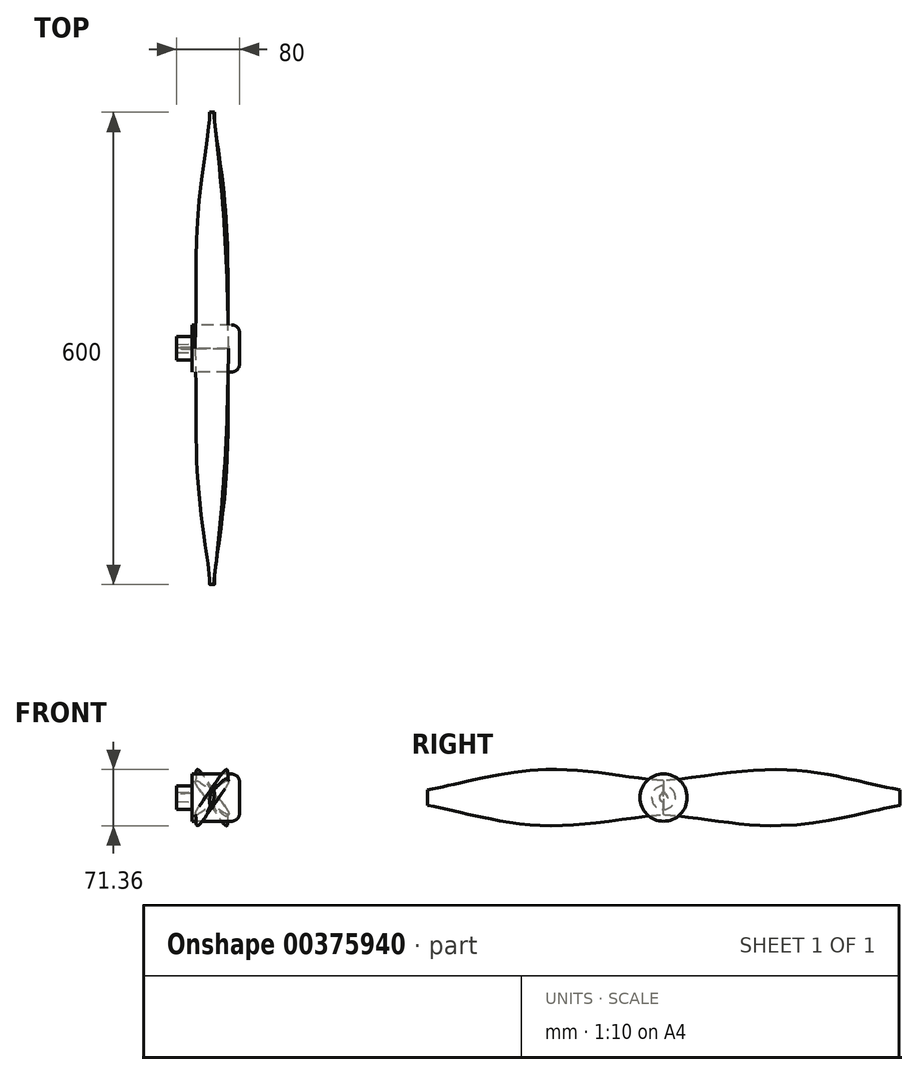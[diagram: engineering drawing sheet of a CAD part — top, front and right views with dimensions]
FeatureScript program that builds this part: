
annotation { "Feature Type Name" : "Feature", "Feature Type Description" : "" }
export const myFeature = defineFeature(function(context is Context, id is Id, definition is map)
    precondition{}
    {
        {
            var Q0;
            Q0=qCreatedBy(makeId("Front.planeOp"),FACE);
            var sketch = newSketch(context, id + "F0", { "sketchPlane" : qUnion([Q0])});
            skEllipse(sketch, "E0", {"center": v(0, 0) * mm, "majorRadius": 30 * mm, "minorRadius": 5 * mm, "majorAxis": v(0.7, 0.7)});
            skLineSegment(sketch, "E1", {"start": v(-3.54, 3.54) * mm, "end": v(3.54, -3.54) * mm, "construction": true});
            skLineSegment(sketch, "E2", {"start": v(-21.21, -21.21) * mm, "end": v(21.21, 21.21) * mm, "construction": true});
            skSolve(sketch);
        }
        {
            assignVariable(context, id + "F1", {"name" : "amplitude", "anyValue" : 300});
        }
        {
            var Q0;
            Q0=qCreatedBy(makeId("Front.planeOp"),FACE);
            cPlane(context, id + "F2", {"entities" : qUnion([Q0]), "cplaneType" : CPlaneType.OFFSET, "offset" : (getVariable(context, 'amplitude') / 2) * mm, "width" : 150 * mm, "height" : 150 * mm});
        }
        {
            var Q0;
            Q0=qCreatedBy(id+"F2.planeOp",FACE);
            var sketch = newSketch(context, id + "F3", { "sketchPlane" : qUnion([Q0])});
            skEllipse(sketch, "E3", {"center": v(0, 0) * mm, "majorRadius": 40 * mm, "minorRadius": 5 * mm, "majorAxis": v(0.46, 0.89)});
            skLineSegment(sketch, "E4", {"start": v(18.47, 35.48) * mm, "end": v(-18.47, -35.48) * mm, "construction": true});
            skLineSegment(sketch, "E5", {"start": v(-4.44, 2.3) * mm, "end": v(4.44, -2.3) * mm, "construction": true});
            skSolve(sketch);
        }
        {
            var Q0;
            Q0=qCreatedBy(makeId("Front.planeOp"),FACE);
            cPlane(context, id + "F4", {"entities" : qUnion([Q0]), "cplaneType" : CPlaneType.OFFSET, "offset" : (getVariable(context, 'amplitude')) * mm, "width" : 150 * mm, "height" : 150 * mm});
        }
        {
            var Q0;
            Q0=qCreatedBy(id+"F4.planeOp",FACE);
            var sketch = newSketch(context, id + "F5", { "sketchPlane" : qUnion([Q0])});
            skEllipse(sketch, "E6", {"center": v(0, 0) * mm, "majorRadius": 10 * mm, "minorRadius": 2.5 * mm, "majorAxis": v(0.17, 0.98)});
            skLineSegment(sketch, "E7", {"start": v(-1.74, -9.85) * mm, "end": v(1.74, 9.85) * mm, "construction": true});
            skLineSegment(sketch, "E8", {"start": v(-2.46, 0.43) * mm, "end": v(2.46, -0.43) * mm, "construction": true});
            skSolve(sketch);
        }
        {
            var Q0;
            Q0=qSketchRegion(id+"F0",true);
            var Q1;
            Q1=qSketchRegion(id+"F3",true);
            var Q2;
            Q2=qSketchRegion(id+"F5",true);
            loft(context, id + "F6", {"sheetProfilesArray" : [{ "sheetProfileEntities" : qUnion([Q0]) }, { "sheetProfileEntities" : qUnion([Q1]) }, { "sheetProfileEntities" : qUnion([Q2]) }]});
        }
        {
            var Q0;
            Q0=qCreatedBy(makeId("Front.planeOp"),FACE);
            var sketch = newSketch(context, id + "F7", { "sketchPlane" : qUnion([Q0])});
            skLineSegment(sketch, "E9", {"start": v(-64.42, 0) * mm, "end": v(60.6, 0) * mm, "construction": true});
            skSolve(sketch);
        }
        {
            var Q0;
            Q0=makeQuery(id+"F6.opLoft","SWEPT_BODY",BODY,{"disambiguationData":[OSD([makeQuery(id+"F0.imprint","IMPRINT",FACE,{"disambiguationData":[TD([[makeQuery(id+"F0.imprint","IMPRINT",EDGE,{"derivedFrom":sQuery(id+"F0.wireOp",EDGE,"E0")}),1.0]])]}),sQuery(id+"F3.wireOp",EDGE,"E3"),makeQuery(id+"F5.imprint","IMPRINT",FACE,{"disambiguationData":[TD([[makeQuery(id+"F5.imprint","IMPRINT",EDGE,{"derivedFrom":sQuery(id+"F5.wireOp",EDGE,"E6")}),1.0]])]})])]});
            var Q1;
            Q1=sQuery(id+"F7.wireOp",EDGE,"E9");
            circularPattern(context, id + "F8", {"entities" : qUnion([Q0]), "axis" : qUnion([Q1]), "angle" : 180 * degree, "instanceCount" : 2, "equalSpace" : true});
        }
        {
            var Q0;
            Q0=qCreatedBy(makeId("Front.planeOp"),FACE);
            var sketch = newSketch(context, id + "F9", { "sketchPlane" : qUnion([Q0])});
            skLineSegment(sketch, "E10", {"start": v(-45, 0) * mm, "end": v(35, 0) * mm});
            skLineSegment(sketch, "E11", {"start": v(35, 0) * mm, "end": v(35, 30) * mm});
            skLineSegment(sketch, "E12", {"start": v(35, 30) * mm, "end": v(-25, 30) * mm});
            skLineSegment(sketch, "E13", {"start": v(-25, 30) * mm, "end": v(-25, 15) * mm});
            skLineSegment(sketch, "E14", {"start": v(-25, 15) * mm, "end": v(-45, 15) * mm});
            skLineSegment(sketch, "E15", {"start": v(-45, 15) * mm, "end": v(-45, 0) * mm});
            skLineSegment(sketch, "E16", {"start": v(-61.67, 0) * mm, "end": v(55.31, 0) * mm, "construction": true});
            skSolve(sketch);
        }
        {
            var Q0;
            Q0=qSketchRegion(id+"F9",true);
            var Q1;
            Q1=sQuery(id+"F9.wireOp",EDGE,"E16");
            revolve(context, id + "F10", {"entities" : qUnion([Q0]), "axis" : qUnion([Q1]), "revolveType" : RevolveType.FULL});
        }
        {
            var Q0;
            Q0=makeQuery(id+"F10.opRevolve","SWEPT_EDGE",EDGE,{"disambiguationData":[OSD([sQuery(id+"F9.wireOp",EDGE,"E11"),sQuery(id+"F9.wireOp",EDGE,"E12")])]});
            fillet(context, id + "F11", {"entities" : qUnion([Q0]), "radius" : 10 * mm, "tangentPropagation" : true, "allowEdgeOverflow" : false});
        }
        {
            var Q0;
            Q0=makeQuery(id+"F10.opRevolve","SWEPT_FACE",FACE,{"disambiguationData":[OSD([sQuery(id+"F9.wireOp",EDGE,"E15")])]});
            var sketch = newSketch(context, id + "F12", { "sketchPlane" : qUnion([Q0])});
            skArc(sketch, "E17", {"start": v(-1, 4.9) * mm, "mid": v(0, -5) * mm, "end": v(1, 4.9) * mm});
            skLineSegment(sketch, "E18.bottom", {"start": v(-1, 6.9) * mm, "end": v(1, 6.9) * mm});
            skLineSegment(sketch, "E18.left", {"start": v(-1, 6.9) * mm, "end": v(-1, 4.9) * mm});
            skLineSegment(sketch, "E18.right", {"start": v(1, 6.9) * mm, "end": v(1, 4.9) * mm});
            skSolve(sketch);
        }
        {
            var Q0;
            Q0=qSketchRegion(id+"F12",true);
            extrude(context, id + "F13", {"entities" : qUnion([Q0]), "operationType" : NewBodyOperationType.REMOVE, "oppositeDirection" : true, "depth" : 20 * mm, "hasDraft" : true, "draftAngle" : 1 * degree});
        }
    });
